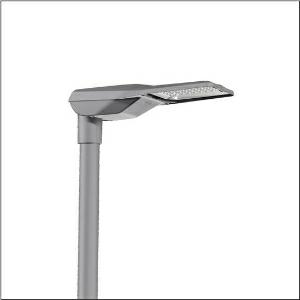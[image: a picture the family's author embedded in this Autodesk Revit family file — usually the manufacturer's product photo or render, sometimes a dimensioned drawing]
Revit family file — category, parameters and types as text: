
# Revit family: streetlight_sl_21_iq_mini___st1_0a_5xe2d41g08gb_82d1
name_source: partatom
category: Lighting Fixtures
units: mm (PartAtom-declared; Revit-internal decimal feet)

## family parameters
Cut with Voids When Loaded = No
Host = Face
Light Source = No
Part Type = Normal
Room Calculation Point = No
Round Connector Dimension = Use Diameter
Shared = No

## types (1)
- --- (1 x LED, 5920 lm, 37.1 W, 4000K)
    Apparent Load = 37 VA
    CIE Flux Codes = 37 72 97 100 100
    Color Rendering = 70
    Color Temperature = 4000K
    Default Elevation = 1800 mm
    Description = Streetlight SL 21 mini, mast luminaire, primary light control with lens, of PMMA, primary optical cover: cover, of toughened safety glass, transparent, light distribution: ST1.0a, light emission: direct distribution, primary light characteristic: asymmetric, installation type: post-top, side-entry, LED, High Power LED, rated luminous flux: 5.920lm, luminous efficacy: 160lm/W, light colour: 740, colour temperature: 4000K, control gear: ECG iQ, control: Street-Remote, Auto-Match, Temp-Guard, Lumen-Switch, Night-Set, Smart-Wire, Light-Fading, Desk-Remote (wireless, voltage-free reading and setting of iQ features in the workshop via application-optimized NFC function/RFID function), optimised constant luminous flux control (CLO 2.0), mains connection: 220..240V, AC, 50/60Hz, start of lifetime: 37W, end of lifetime: 39W, reduction: 18W, luminaire housing, of diecast aluminium, powder-coated, Siteco® metallic grey (DB 702S), corrosivity category C5 according to DIN EN ISO 12944, length: 628mm, width: 235mm, height: 110mm, spigot size: 60/76mm (post-top) and 42/60/76mm (side-entry), mast flange for spigot size: 42mm: 5XC10008XM4, 60mm: 5XC10008XM2, 76/60mm: 5XC10108XM1, protection rating (complete): IP66, insulation class (complete): insulation class II (safety insulation), certification: CE, ENEC, VDE, impact resistance: IK09, permissible operating ambient temperature for outdoor applications: -40..+50°C, standard-compliant lighting for roads and squares, packaging unit: 1 piece

Light Distribution: ST1.0a
    Height = 110 mm
    Lamp = 1 x LED
    Lamp Light Flux = 5920 lm
    Lamp Power = 37.1 W
    Lamp count = 1
    Length = 625 mm
    Luminous efficacy = 160 lm/W
    Manufacturer = Siteco
    ModVariant = No
    Model = 5XE2D41G08GB
    Number of Poles = 1
    OnlyDefault = Yes
    Power Factor = 1
    Product Name = Streetlight SL 21 iQ mini | ST1.0a
    Product group = mast luminaire | pylon top
    ProductGroupID = 6100
    Protection Class = Protection class II
    Protection Degree = IP 66
    RLX_Detail_Level = 1
    RlxData = <blob elided: 92149 chars, md5=04c0ef5c>
    Socket = socket
    Standby Power = 0 W
    System Light Flux = 5920 lm
    System Power = 37 W
    Type Comments = factory setting: luminous flux: 100 % | dim-lin: 254 | 385 mA
    Type Image = l_1003519.jpg
    URL = http://relux.com
    VarID = @adj_107111
    Voltage = 0 V
    Weight = 0.00 kg
    Width = 234 mm

## geometry (parser evidence)
native form markers: Blend x4, Sweep x11
no freeform markers — native parametric forms only
